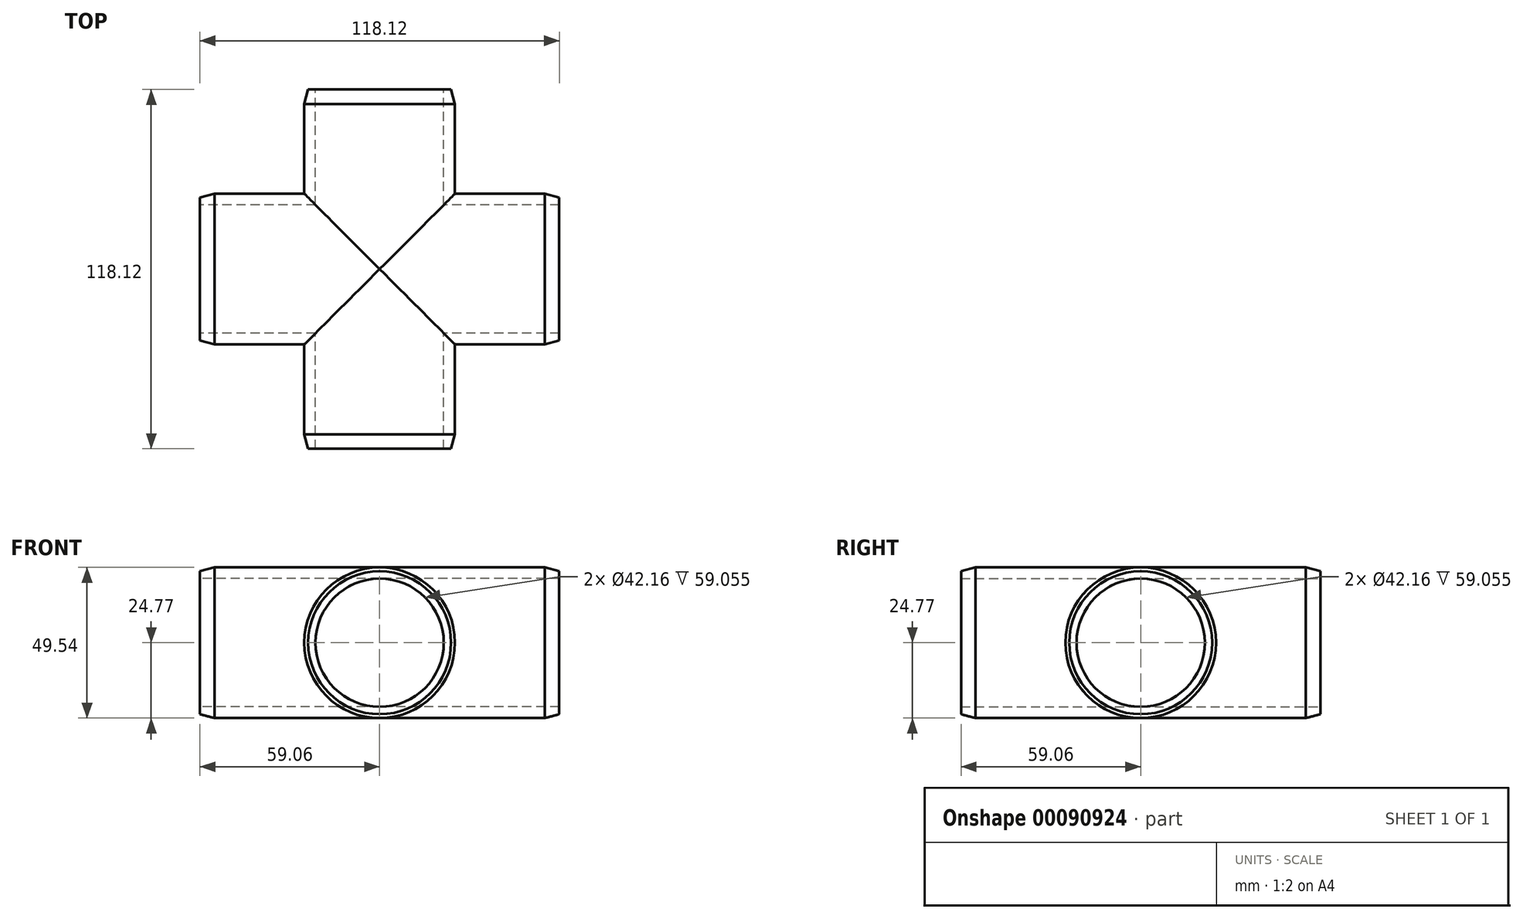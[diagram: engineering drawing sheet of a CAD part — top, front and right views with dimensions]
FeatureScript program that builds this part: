
annotation { "Feature Type Name" : "Feature", "Feature Type Description" : "" }
export const myFeature = defineFeature(function(context is Context, id is Id, definition is map)
    precondition{}
    {
        {
            var Q0;
            Q0=qCreatedBy(makeId("Front.planeOp"),FACE);
            var sketch = newSketch(context, id + "F0", { "sketchPlane" : qUnion([Q0])});
            skCircle(sketch, "E0", {"center": v(0, 0) * mm, "radius": 21.08 * mm});
            skCircle(sketch, "E1.0", {"center": v(0, 0) * mm, "radius": 24.77 * mm});
            skSolve(sketch);
        }
        {
            var Q0;
            Q0=qSketchRegion(id+"F0",true);
            extrude(context, id + "F1", {"entities" : qUnion([Q0]), "endBound" : BoundingType.SYMMETRIC, "depth" : 118.11 * mm});
        }
        {
            var Q0;
            Q0=qCreatedBy(makeId("Right.planeOp"),FACE);
            var sketch = newSketch(context, id + "F2", { "sketchPlane" : qUnion([Q0])});
            skCircle(sketch, "E2", {"center": v(0, 0) * mm, "radius": 21.08 * mm});
            skCircle(sketch, "E3.0", {"center": v(0, 0) * mm, "radius": 24.77 * mm});
            skSolve(sketch);
        }
        {
            var Q0;
            Q0=qSketchRegion(id+"F2",true);
            extrude(context, id + "F3", {"entities" : qUnion([Q0]), "operationType" : NewBodyOperationType.ADD, "endBound" : BoundingType.SYMMETRIC, "depth" : 118.11 * mm});
        }
        {
            var Q0;
            Q0=makeQuery(id+"F2.imprint","IMPRINT",FACE,{"disambiguationData":[TD([[makeQuery(id+"F2.imprint","IMPRINT",EDGE,{"derivedFrom":sQuery(id+"F2.wireOp",EDGE,"E2")}),1.0]])]});
            extrude(context, id + "F4", {"entities" : qUnion([Q0]), "operationType" : NewBodyOperationType.REMOVE, "endBound" : BoundingType.THROUGH_ALL, "depth" : 25.4 * mm, "hasSecondDirection" : true, "secondDirectionBound" : SecondDirectionBoundingType.THROUGH_ALL, "secondDirectionOppositeDirection" : true, "secondDirectionDepth" : 25.4 * mm});
        }
        {
            var Q0;
            Q0=makeQuery(id+"F0.imprint","IMPRINT",FACE,{"disambiguationData":[TD([[makeQuery(id+"F0.imprint","IMPRINT",EDGE,{"derivedFrom":sQuery(id+"F0.wireOp",EDGE,"E0")}),1.0]])]});
            extrude(context, id + "F5", {"entities" : qUnion([Q0]), "operationType" : NewBodyOperationType.REMOVE, "endBound" : BoundingType.THROUGH_ALL, "depth" : 25.4 * mm, "hasSecondDirection" : true, "secondDirectionBound" : SecondDirectionBoundingType.THROUGH_ALL, "secondDirectionOppositeDirection" : true, "secondDirectionDepth" : 25.4 * mm});
        }
        {
            var Q0;
            Q0=makeQuery(id+"FafeMV82ZdMxNU9_1.opExtrude","CAP_EDGE",EDGE,{"disambiguationData":[OSD([sQuery(id+"FKzl36Kfq815hOB_1.wireOp",EDGE,"0c5890f9-7e0d-4e56-9e25-773390a1f3e3.0")])],"isStart":false});
            var Q1;
            Q1=makeQuery(id+"F1.opExtrude","CAP_EDGE",EDGE,{"disambiguationData":[OSD([sQuery(id+"F0.wireOp",EDGE,"E1.0")])],"isStart":false});
            var Q2;
            Q2=makeQuery(id+"F3.opExtrude","CAP_EDGE",EDGE,{"disambiguationData":[OSD([sQuery(id+"F2.wireOp",EDGE,"E3.0")])],"isStart":false});
            chamfer(context, id + "F6", {"entities" : qUnion([Q0, Q1, Q2]), "chamferType" : ChamferType.OFFSET_ANGLE, "width" : 1.27 * mm, "oppositeDirection" : false, "angle" : 75 * degree, "tangentPropagation" : true});
        }
        {
            var Q0;
            Q0=makeQuery(id+"F1.opExtrude","CAP_EDGE",EDGE,{"disambiguationData":[OSD([sQuery(id+"F0.wireOp",EDGE,"E1.0")])],"isStart":true});
            var Q1;
            Q1=makeQuery(id+"F3.opExtrude","CAP_EDGE",EDGE,{"disambiguationData":[OSD([sQuery(id+"F2.wireOp",EDGE,"E3.0")])],"isStart":true});
            chamfer(context, id + "F7", {"entities" : qUnion([Q0, Q1]), "chamferType" : ChamferType.OFFSET_ANGLE, "width" : 1.27 * mm, "oppositeDirection" : true, "angle" : 75 * degree, "tangentPropagation" : true});
        }
    });
